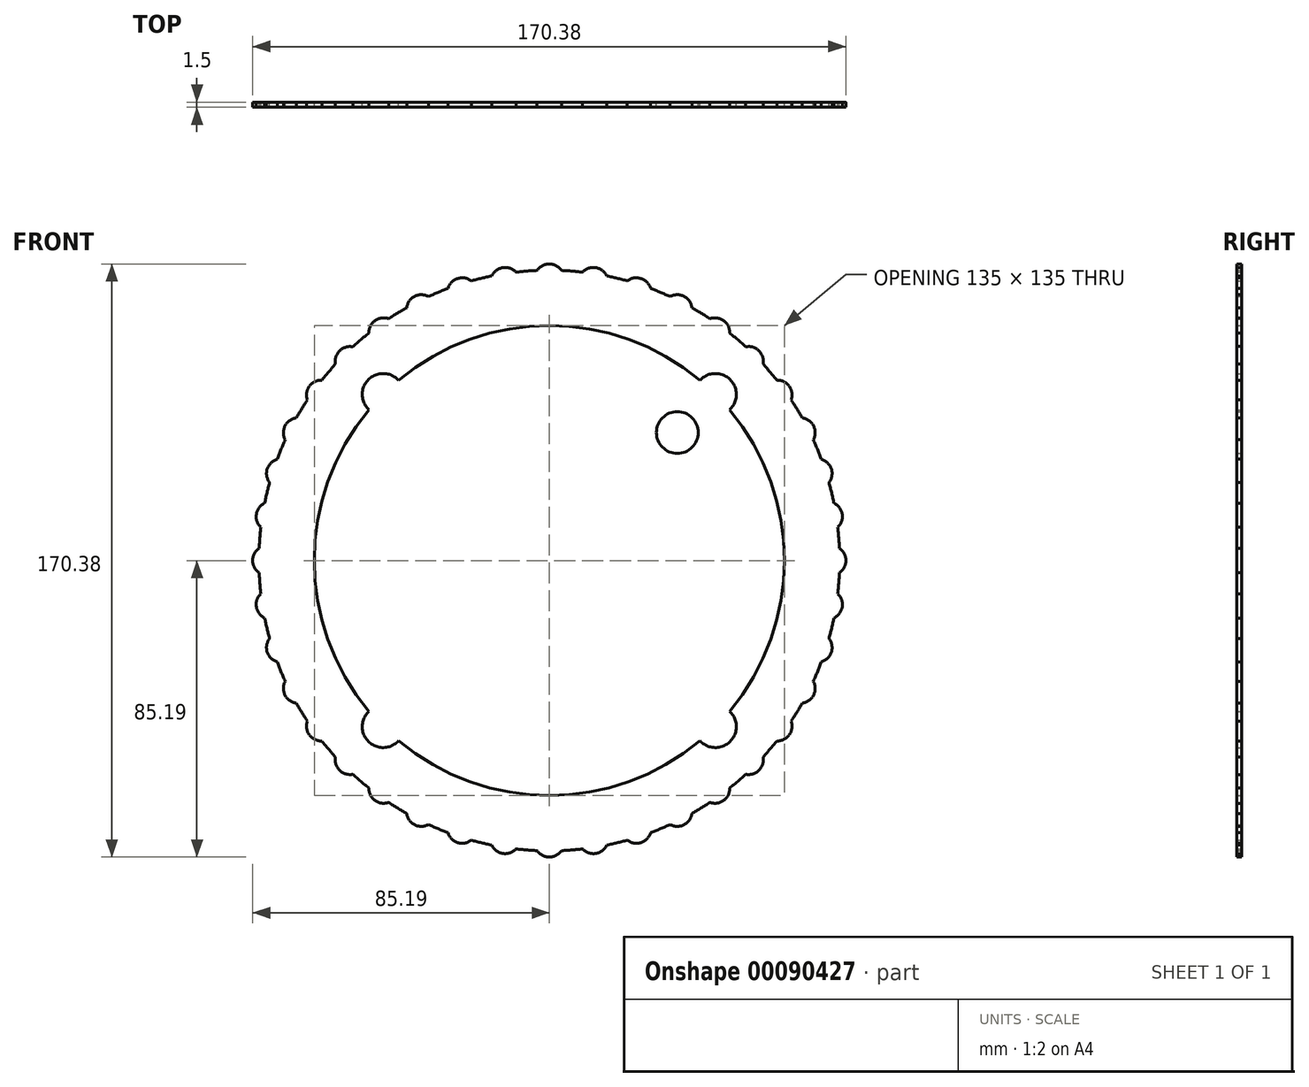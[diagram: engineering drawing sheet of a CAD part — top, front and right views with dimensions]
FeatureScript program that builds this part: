
annotation { "Feature Type Name" : "Feature", "Feature Type Description" : "" }
export const myFeature = defineFeature(function(context is Context, id is Id, definition is map)
    precondition{}
    {
        {
            var Q0;
            Q0=qCreatedBy(makeId("Front.planeOp"),FACE);
            var sketch = newSketch(context, id + "F0", { "sketchPlane" : qUnion([Q0])});
            skCircle(sketch, "E0", {"center": v(0, 0) * mm, "radius": 52 * mm});
            skCircle(sketch, "E1", {"center": v(0, 0) * mm, "radius": 67.5 * mm});
            skLineSegment(sketch, "E2", {"start": v(0, 0) * mm, "end": v(0, 67.5) * mm, "construction": true});
            skLineSegment(sketch, "E3", {"start": v(0, 67.5) * mm, "end": v(0, 0) * mm, "construction": true});
            skLineSegment(sketch, "E4", {"start": v(47.73, 47.73) * mm, "end": v(-47.73, -47.73) * mm, "construction": true});
            skCircle(sketch, "E5", {"center": v(36.77, 36.77) * mm, "radius": 6 * mm});
            skCircle(sketch, "E6", {"center": v(47.73, 47.73) * mm, "radius": 6 * mm});
            skLineSegment(sketch, "E7", {"start": v(-47.73, 47.73) * mm, "end": v(47.73, -47.73) * mm, "construction": true});
            skPoint(sketch, "E8.orphan", {"position": v(56.34, -56.34) * mm});
            skCircle(sketch, "E9", {"center": v(-47.73, 47.73) * mm, "radius": 6 * mm});
            skCircle(sketch, "E10", {"center": v(-47.73, -47.73) * mm, "radius": 6 * mm});
            skCircle(sketch, "E11", {"center": v(47.73, -47.73) * mm, "radius": 6 * mm});
            skCircle(sketch, "E12", {"center": v(36.77, -36.77) * mm, "radius": 6 * mm});
            skCircle(sketch, "E13", {"center": v(-36.77, -36.77) * mm, "radius": 6 * mm});
            skCircle(sketch, "E14", {"center": v(-36.77, 36.77) * mm, "radius": 6 * mm});
            skCircle(sketch, "E15", {"center": v(0, 0) * mm, "radius": 83.4 * mm});
            skCircle(sketch, "E16", {"center": v(0, 0) * mm, "radius": 80.94 * mm, "construction": true});
            skCircle(sketch, "E17", {"center": v(0, 80.94) * mm, "radius": 4.25 * mm});
            skCircle(sketch, "E18.1.0", {"center": v(-12.66, 79.94) * mm, "radius": 4.25 * mm});
            skCircle(sketch, "E18.2.0", {"center": v(-25.01, 76.97) * mm, "radius": 4.25 * mm});
            skCircle(sketch, "E18.3.0", {"center": v(-36.74, 72.11) * mm, "radius": 4.25 * mm});
            skCircle(sketch, "E18.4.0", {"center": v(-47.57, 65.48) * mm, "radius": 4.25 * mm});
            skCircle(sketch, "E18.5.0", {"center": v(-57.23, 57.23) * mm, "radius": 4.25 * mm});
            skCircle(sketch, "E18.6.0", {"center": v(-65.48, 47.57) * mm, "radius": 4.25 * mm});
            skCircle(sketch, "E18.7.0", {"center": v(-72.11, 36.74) * mm, "radius": 4.25 * mm});
            skCircle(sketch, "E18.8.0", {"center": v(-76.97, 25.01) * mm, "radius": 4.25 * mm});
            skCircle(sketch, "E18.9.0", {"center": v(-79.94, 12.66) * mm, "radius": 4.25 * mm});
            skCircle(sketch, "E18.10.0", {"center": v(-80.94, 0) * mm, "radius": 4.25 * mm});
            skCircle(sketch, "E18.11.0", {"center": v(-79.94, -12.66) * mm, "radius": 4.25 * mm});
            skCircle(sketch, "E18.12.0", {"center": v(-76.97, -25.01) * mm, "radius": 4.25 * mm});
            skCircle(sketch, "E18.13.0", {"center": v(-72.11, -36.74) * mm, "radius": 4.25 * mm});
            skCircle(sketch, "E18.14.0", {"center": v(-65.48, -47.57) * mm, "radius": 4.25 * mm});
            skCircle(sketch, "E18.15.0", {"center": v(-57.23, -57.23) * mm, "radius": 4.25 * mm});
            skCircle(sketch, "E18.16.0", {"center": v(-47.57, -65.48) * mm, "radius": 4.25 * mm});
            skCircle(sketch, "E18.17.0", {"center": v(-36.74, -72.11) * mm, "radius": 4.25 * mm});
            skCircle(sketch, "E18.18.0", {"center": v(-25.01, -76.97) * mm, "radius": 4.25 * mm});
            skCircle(sketch, "E18.19.0", {"center": v(-12.66, -79.94) * mm, "radius": 4.25 * mm});
            skCircle(sketch, "E18.20.0", {"center": v(0, -80.94) * mm, "radius": 4.25 * mm});
            skCircle(sketch, "E18.21.0", {"center": v(12.66, -79.94) * mm, "radius": 4.25 * mm});
            skCircle(sketch, "E18.22.0", {"center": v(25.01, -76.97) * mm, "radius": 4.25 * mm});
            skCircle(sketch, "E18.23.0", {"center": v(36.74, -72.11) * mm, "radius": 4.25 * mm});
            skCircle(sketch, "E18.24.0", {"center": v(47.57, -65.48) * mm, "radius": 4.25 * mm});
            skCircle(sketch, "E18.25.0", {"center": v(57.23, -57.23) * mm, "radius": 4.25 * mm});
            skCircle(sketch, "E18.26.0", {"center": v(65.48, -47.57) * mm, "radius": 4.25 * mm});
            skCircle(sketch, "E18.27.0", {"center": v(72.11, -36.74) * mm, "radius": 4.25 * mm});
            skCircle(sketch, "E18.28.0", {"center": v(76.97, -25.01) * mm, "radius": 4.25 * mm});
            skCircle(sketch, "E18.29.0", {"center": v(79.94, -12.66) * mm, "radius": 4.25 * mm});
            skCircle(sketch, "E18.30.0", {"center": v(80.94, 0) * mm, "radius": 4.25 * mm});
            skCircle(sketch, "E18.31.0", {"center": v(79.94, 12.66) * mm, "radius": 4.25 * mm});
            skCircle(sketch, "E18.32.0", {"center": v(76.97, 25.01) * mm, "radius": 4.25 * mm});
            skCircle(sketch, "E18.33.0", {"center": v(72.11, 36.74) * mm, "radius": 4.25 * mm});
            skCircle(sketch, "E18.34.0", {"center": v(65.48, 47.57) * mm, "radius": 4.25 * mm});
            skCircle(sketch, "E18.35.0", {"center": v(57.23, 57.23) * mm, "radius": 4.25 * mm});
            skCircle(sketch, "E18.36.0", {"center": v(47.57, 65.48) * mm, "radius": 4.25 * mm});
            skCircle(sketch, "E18.37.0", {"center": v(36.74, 72.11) * mm, "radius": 4.25 * mm});
            skCircle(sketch, "E18.38.0", {"center": v(25.01, 76.97) * mm, "radius": 4.25 * mm});
            skCircle(sketch, "E18.39.0", {"center": v(12.66, 79.94) * mm, "radius": 4.25 * mm});
            skSolve(sketch);
        }
        {
            var Q0;
            Q0 = qSketchRegion(id + "F0", true);
            var Q1;
            {var subQ5=sQuery(id+"F0.wireOp",EDGE,"E5");var subQ6=sQuery(id+"F0.wireOp",EDGE,"E0");var subQ7=makeQuery(id+"F0.imprint","INTERSECT",VERTEX,{"disambiguationData":[OD(0.0)],"derivedFrom":[subQ6,subQ5]});Q1=makeQuery(id+"F0.imprint","IMPRINT",FACE,{"disambiguationData":[TD([[makeQuery(id+"F0.imprint","IMPRINT",EDGE,{"disambiguationData":[TD([[subQ7,-1.0]])],"derivedFrom":subQ6}),-1.0]])]});}
            var Q2;
            {var subQ0=sQuery(id+"F0.wireOp",EDGE,"E5");var subQ1=sQuery(id+"F0.wireOp",EDGE,"E0");var subQ8=makeQuery(id+"F0.imprint","INTERSECT",VERTEX,{"disambiguationData":[OD(0.0)],"derivedFrom":[subQ1,subQ0]});Q2=makeQuery(id+"F0.imprint","IMPRINT",FACE,{"disambiguationData":[TD([[makeQuery(id+"F0.imprint","IMPRINT",EDGE,{"disambiguationData":[TD([[subQ8,-1.0]])],"derivedFrom":subQ1}),1.0]])]});}
            extrude(context, id + "F1", {"entities" : qUnion([Q0, Q1, Q2]), "endBound" : BoundingType.SYMMETRIC, "depth" : 1.5 * mm});
        }
    });
